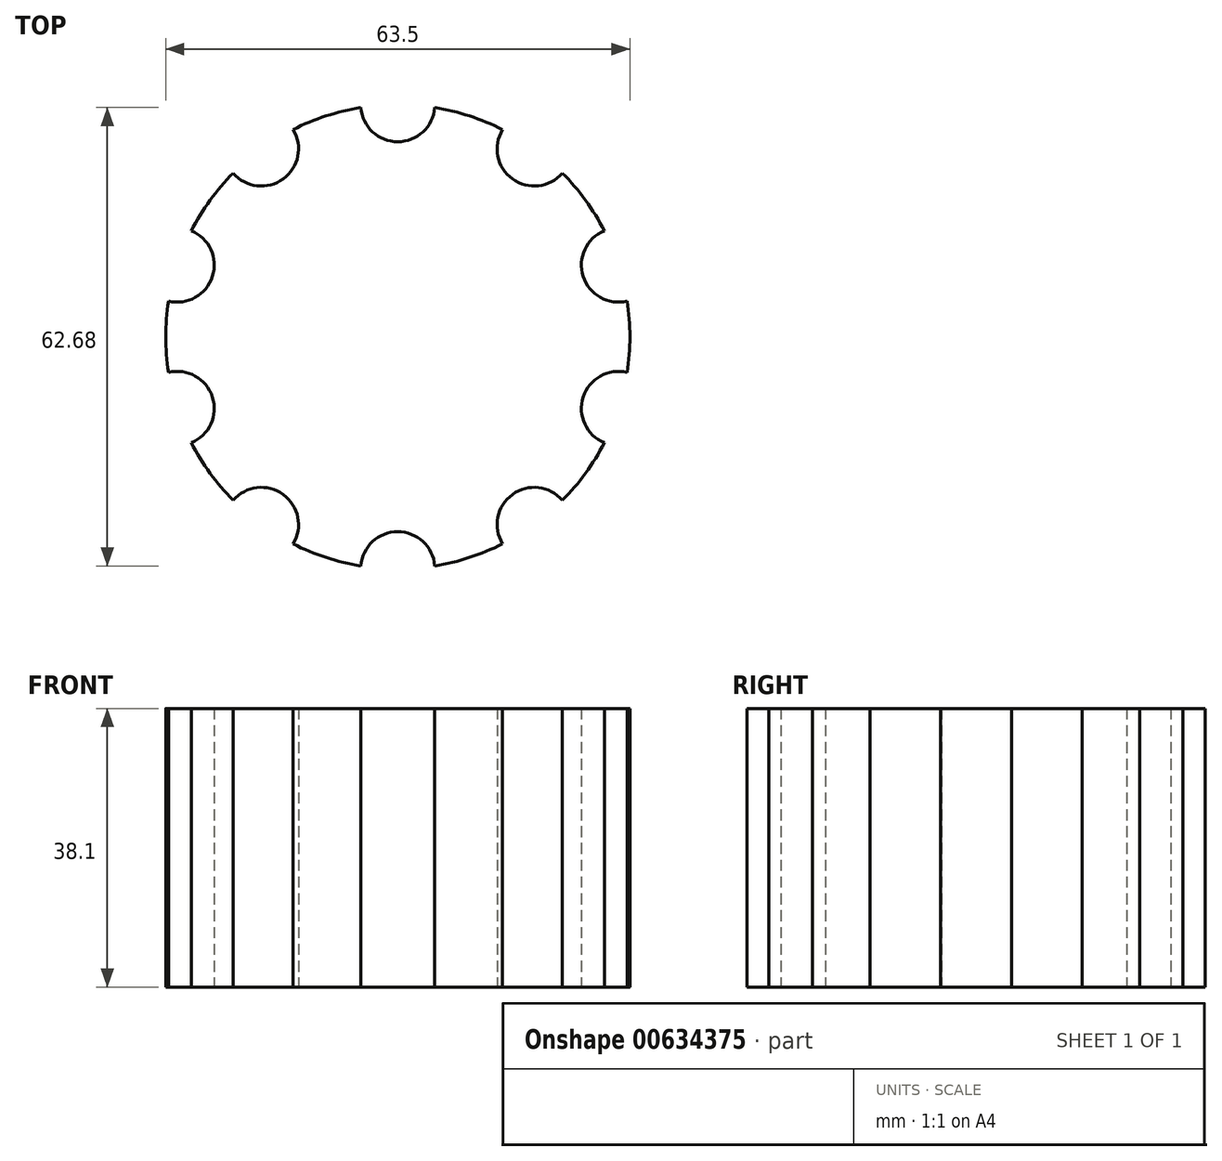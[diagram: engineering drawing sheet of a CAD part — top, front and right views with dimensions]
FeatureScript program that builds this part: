
annotation { "Feature Type Name" : "Feature", "Feature Type Description" : "" }
export const myFeature = defineFeature(function(context is Context, id is Id, definition is map)
    precondition{}
    {
        {
            var Q0;
            Q0=qCreatedBy(makeId("Top.planeOp"),FACE);
            var sketch = newSketch(context, id + "F0", { "sketchPlane" : qUnion([Q0])});
            skCircle(sketch, "E0", {"center": v(0, 0) * mm, "radius": 31.75 * mm});
            skSolve(sketch);
        }
        {
            var Q0;
            Q0=makeQuery(id+"F0.imprint","IMPRINT",FACE,{"disambiguationData":[TD([[makeQuery(id+"F0.imprint","IMPRINT",EDGE,{"derivedFrom":sQuery(id+"F0.wireOp",EDGE,"E0")}),1.0]])]});
            extrude(context, id + "F1", {"entities" : qUnion([Q0]), "depth" : 38.1 * mm});
        }
        {
            var Q0;
            Q0=qCreatedBy(makeId("Top.planeOp"),FACE);
            var sketch = newSketch(context, id + "F2", { "sketchPlane" : qUnion([Q0])});
            skCircle(sketch, "E1", {"center": v(0, 31.75) * mm, "radius": 5.08 * mm});
            skCircle(sketch, "E2.1.0", {"center": v(-18.66, 25.69) * mm, "radius": 5.08 * mm});
            skCircle(sketch, "E2.2.0", {"center": v(-30.2, 9.81) * mm, "radius": 5.08 * mm});
            skCircle(sketch, "E2.3.0", {"center": v(-30.2, -9.81) * mm, "radius": 5.08 * mm});
            skCircle(sketch, "E2.4.0", {"center": v(-18.66, -25.69) * mm, "radius": 5.08 * mm});
            skCircle(sketch, "E2.5.0", {"center": v(0, -31.75) * mm, "radius": 5.08 * mm});
            skCircle(sketch, "E2.6.0", {"center": v(18.66, -25.69) * mm, "radius": 5.08 * mm});
            skCircle(sketch, "E2.7.0", {"center": v(30.2, -9.81) * mm, "radius": 5.08 * mm});
            skCircle(sketch, "E2.8.0", {"center": v(30.2, 9.81) * mm, "radius": 5.08 * mm});
            skCircle(sketch, "E2.9.0", {"center": v(18.66, 25.69) * mm, "radius": 5.08 * mm});
            skPoint(sketch, "E2.center", {"position": v(0, 0) * mm});
            skSolve(sketch);
        }
        {
            var Q0;
            Q0=qSketchRegion(id+"F2",true);
            extrude(context, id + "F3", {"entities" : qUnion([Q0]), "depth" : 50.8 * mm});
        }
        {
            var Q0;
            Q0=makeQuery(id+"F3.opExtrude","SWEPT_BODY",BODY,{"disambiguationData":[OSD([sQuery(id+"F2.wireOp",EDGE,"E2.7.0")])]});
            var Q1;
            Q1=makeQuery(id+"F3.opExtrude","SWEPT_BODY",BODY,{"disambiguationData":[OSD([sQuery(id+"F2.wireOp",EDGE,"E2.6.0")])]});
            var Q2;
            Q2=makeQuery(id+"F3.opExtrude","SWEPT_BODY",BODY,{"disambiguationData":[OSD([sQuery(id+"F2.wireOp",EDGE,"E2.5.0")])]});
            var Q3;
            Q3=makeQuery(id+"F3.opExtrude","SWEPT_BODY",BODY,{"disambiguationData":[OSD([sQuery(id+"F2.wireOp",EDGE,"E2.4.0")])]});
            var Q4;
            Q4=makeQuery(id+"F3.opExtrude","SWEPT_BODY",BODY,{"disambiguationData":[OSD([sQuery(id+"F2.wireOp",EDGE,"E2.3.0")])]});
            var Q5;
            Q5=makeQuery(id+"F3.opExtrude","SWEPT_BODY",BODY,{"disambiguationData":[OSD([sQuery(id+"F2.wireOp",EDGE,"E2.2.0")])]});
            var Q6;
            Q6=makeQuery(id+"F3.opExtrude","SWEPT_BODY",BODY,{"disambiguationData":[OSD([sQuery(id+"F2.wireOp",EDGE,"E2.1.0")])]});
            var Q7;
            Q7=makeQuery(id+"F3.opExtrude","SWEPT_BODY",BODY,{"disambiguationData":[OSD([sQuery(id+"F2.wireOp",EDGE,"E1")])]});
            var Q8;
            Q8=makeQuery(id+"F3.opExtrude","SWEPT_BODY",BODY,{"disambiguationData":[OSD([sQuery(id+"F2.wireOp",EDGE,"E2.9.0")])]});
            var Q9;
            Q9=makeQuery(id+"F3.opExtrude","SWEPT_BODY",BODY,{"disambiguationData":[OSD([sQuery(id+"F2.wireOp",EDGE,"E2.8.0")])]});
            var Q10;
            Q10=makeQuery(id+"F1.opExtrude","SWEPT_BODY",BODY,{"disambiguationData":[OSD([sQuery(id+"F0.wireOp",EDGE,"E0")])]});
            booleanBodies(context, id + "F4", {"operationType" : BooleanOperationType.SUBTRACTION, "tools" : qUnion([Q0, Q1, Q2, Q3, Q4, Q5, Q6, Q7, Q8, Q9]), "targets" : qUnion([Q10])});
        }
    });
